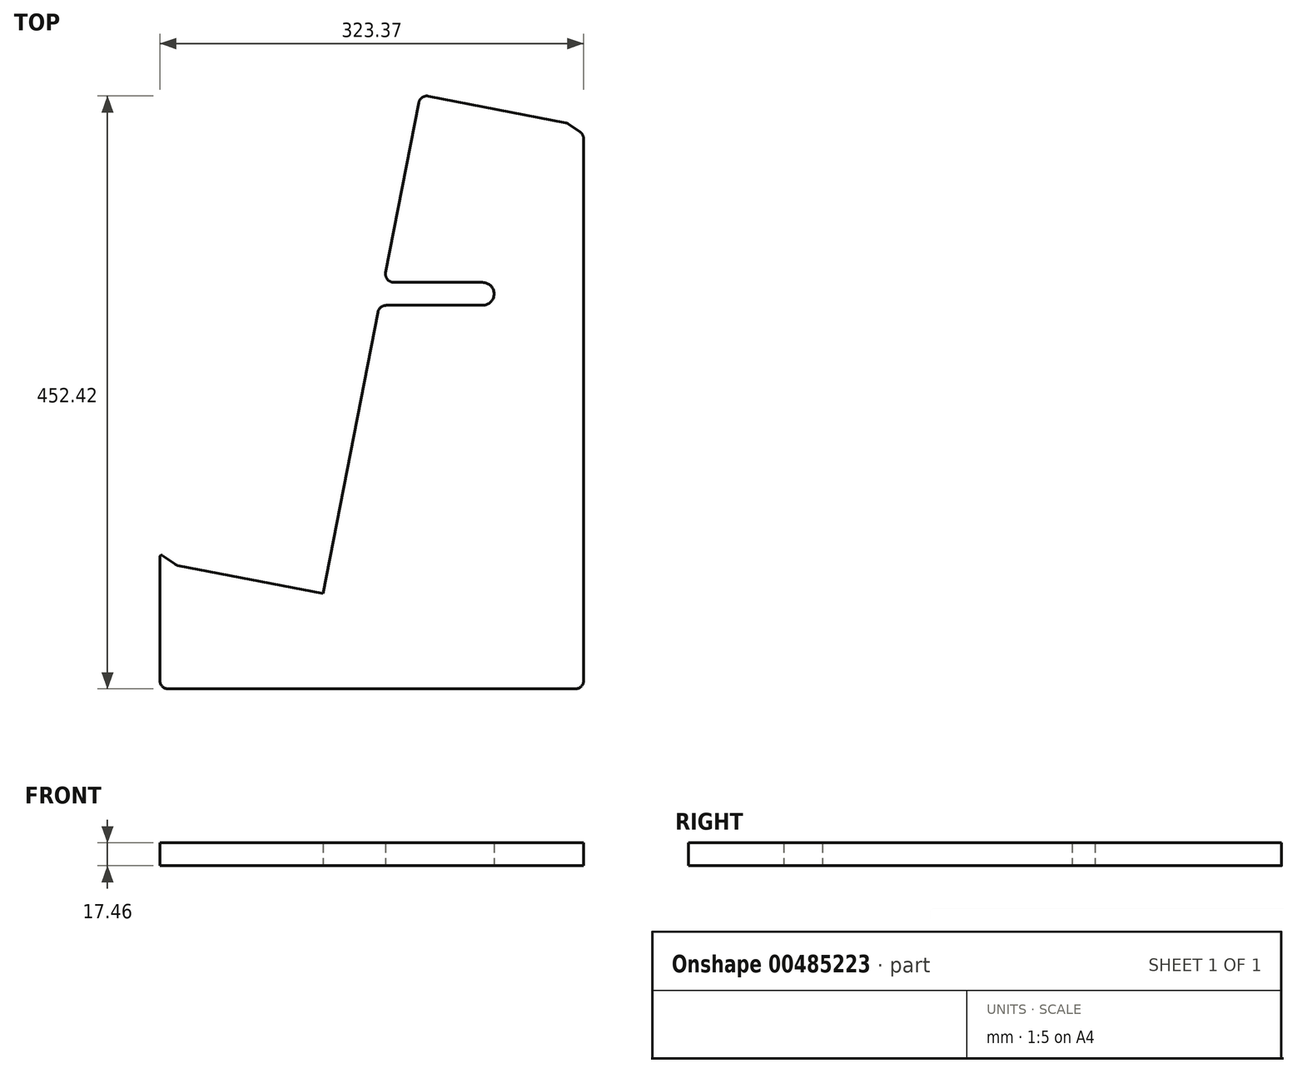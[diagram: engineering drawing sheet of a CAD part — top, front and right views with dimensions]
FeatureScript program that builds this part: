
annotation { "Feature Type Name" : "Feature", "Feature Type Description" : "" }
export const myFeature = defineFeature(function(context is Context, id is Id, definition is map)
    precondition{}
    {
        {
            var Q0;
            Q0=qCreatedBy(makeId("Top.planeOp"),FACE);
            var sketch = newSketch(context, id + "F0", { "sketchPlane" : qUnion([Q0])});
            skLineSegment(sketch, "E0", {"start": v(-95.53, 76.65) * mm, "end": v(-95.53, -96.88) * mm, "construction": true});
            skLineSegment(sketch, "E1", {"start": v(-95.53, -96.88) * mm, "end": v(232.75, -96.88) * mm, "construction": true});
            skLineSegment(sketch, "E2", {"start": v(-95.53, 0) * mm, "end": v(131.9, -44.2) * mm, "construction": true});
            skPoint(sketch, "E3", {"position": v(29.14, -24.23) * mm});
            skLineSegment(sketch, "E4", {"start": v(29.14, -24.23) * mm, "end": v(177.2, 737.5) * mm, "construction": true});
            skPoint(sketch, "E5", {"position": v(-83.06, -2.42) * mm});
            skPoint(sketch, "E6", {"position": v(-95.53, 6.35) * mm});
            skLineSegment(sketch, "E7", {"start": v(50.97, 195.8) * mm, "end": v(227.84, 195.8) * mm, "construction": true});
            skLineSegment(sketch, "E8", {"start": v(55.86, 213.27) * mm, "end": v(227.84, 213.27) * mm, "construction": true});
            skPoint(sketch, "E9", {"position": v(71.91, 195.8) * mm});
            skPoint(sketch, "E10", {"position": v(75.3, 213.27) * mm});
            skPoint(sketch, "E11", {"position": v(103.17, 356.63) * mm});
            skLineSegment(sketch, "E12", {"start": v(103.17, 356.63) * mm, "end": v(227.84, 332.4) * mm, "construction": true});
            skLineSegment(sketch, "E13", {"start": v(227.84, 332.4) * mm, "end": v(227.84, -191.89) * mm, "construction": true});
            skLineSegment(sketch, "E14", {"start": v(241.78, 204.54) * mm, "end": v(61.61, 204.54) * mm, "construction": true});
            skPoint(sketch, "E15", {"position": v(73.6, 204.54) * mm});
            skPoint(sketch, "E16", {"position": v(227.84, 204.54) * mm});
            skPoint(sketch, "E17", {"position": v(150.73, 204.54) * mm});
            skArc(sketch, "E18", {"start": v(150.73, 195.8) * mm, "mid": v(159.46, 204.54) * mm, "end": v(150.73, 213.27) * mm});
            skLineSegment(sketch, "E19", {"start": v(-93.53, 4.94) * mm, "end": v(-84.17, -1.64) * mm});
            skLineSegment(sketch, "E20", {"start": v(-95.53, 3.9) * mm, "end": v(-95.53, -90.53) * mm});
            skLineSegment(sketch, "E21", {"start": v(-81.73, -2.68) * mm, "end": v(29.14, -24.23) * mm});
            skLineSegment(sketch, "E22", {"start": v(70.91, 190.67) * mm, "end": v(29.14, -24.23) * mm});
            skLineSegment(sketch, "E23", {"start": v(77.15, 195.8) * mm, "end": v(150.73, 195.8) * mm});
            skLineSegment(sketch, "E24", {"start": v(150.73, 213.27) * mm, "end": v(83, 213.27) * mm});
            skPoint(sketch, "E25", {"position": v(227.84, 326.05) * mm});
            skPoint(sketch, "E26", {"position": v(215.37, 334.82) * mm});
            skLineSegment(sketch, "E27", {"start": v(225.14, 327.95) * mm, "end": v(216.48, 334.04) * mm});
            skLineSegment(sketch, "E28", {"start": v(214.04, 335.08) * mm, "end": v(109.4, 355.42) * mm});
            skLineSegment(sketch, "E29", {"start": v(101.96, 350.4) * mm, "end": v(76.78, 220.83) * mm});
            skLineSegment(sketch, "E30", {"start": v(227.84, 322.75) * mm, "end": v(227.84, -90.53) * mm});
            skLineSegment(sketch, "E31", {"start": v(-89.18, -96.88) * mm, "end": v(221.49, -96.88) * mm});
            skArc(sketch, "E32.filletArc", {"start": v(77.15, 195.8) * mm, "mid": v(73.1, 194.35) * mm, "end": v(70.91, 190.67) * mm});
            skArc(sketch, "E33.filletArc", {"start": v(76.78, 220.83) * mm, "mid": v(78.1, 215.58) * mm, "end": v(83, 213.27) * mm});
            skArc(sketch, "E34.filletArc", {"start": v(109.4, 355.42) * mm, "mid": v(104.64, 354.45) * mm, "end": v(101.96, 350.4) * mm});
            skArc(sketch, "E35.filletArc", {"start": v(216.48, 334.04) * mm, "mid": v(215.32, 334.7) * mm, "end": v(214.04, 335.08) * mm});
            skArc(sketch, "E36.filletArc", {"start": v(227.84, 322.75) * mm, "mid": v(227.13, 325.68) * mm, "end": v(225.14, 327.95) * mm});
            skPoint(sketch, "E37.visualSharp", {"position": v(227.84, -96.88) * mm});
            skArc(sketch, "E37.filletArc", {"start": v(221.49, -96.88) * mm, "mid": v(225.98, -95.02) * mm, "end": v(227.84, -90.53) * mm});
            skPoint(sketch, "E38.visualSharp", {"position": v(-95.53, -96.88) * mm});
            skArc(sketch, "E38.filletArc", {"start": v(-95.53, -90.53) * mm, "mid": v(-93.67, -95.02) * mm, "end": v(-89.18, -96.88) * mm});
            skArc(sketch, "E39.filletArc", {"start": v(-93.53, 4.94) * mm, "mid": v(-94.84, 5.03) * mm, "end": v(-95.53, 3.9) * mm});
            skArc(sketch, "E40.filletArc", {"start": v(-84.17, -1.64) * mm, "mid": v(-83, -2.3) * mm, "end": v(-81.73, -2.68) * mm});
            skSolve(sketch);
        }
        {
            var Q0;
            Q0 = qSketchRegion(id + "F0", true);
            extrude(context, id + "F1", {"entities" : qUnion([Q0]), "depth" : 17.46 * mm});
        }
        {
            var Q0;
            Q0=makeQuery(id+"F1.opExtrude","SWEPT_BODY",BODY,{"disambiguationData":[OSD([sQuery(id+"F0.wireOp",EDGE,"E18"),sQuery(id+"F0.wireOp",EDGE,"E19"),sQuery(id+"F0.wireOp",EDGE,"E20"),sQuery(id+"F0.wireOp",EDGE,"E21"),sQuery(id+"F0.wireOp",EDGE,"E22"),sQuery(id+"F0.wireOp",EDGE,"E23"),sQuery(id+"F0.wireOp",EDGE,"E24"),sQuery(id+"F0.wireOp",EDGE,"E27"),sQuery(id+"F0.wireOp",EDGE,"E28"),sQuery(id+"F0.wireOp",EDGE,"E29"),sQuery(id+"F0.wireOp",EDGE,"E30"),sQuery(id+"F0.wireOp",EDGE,"E31"),sQuery(id+"F0.wireOp",EDGE,"E32.filletArc"),sQuery(id+"F0.wireOp",EDGE,"E33.filletArc"),sQuery(id+"F0.wireOp",EDGE,"E34.filletArc"),sQuery(id+"F0.wireOp",EDGE,"E35.filletArc"),sQuery(id+"F0.wireOp",EDGE,"E36.filletArc"),sQuery(id+"F0.wireOp",EDGE,"E37.filletArc"),sQuery(id+"F0.wireOp",EDGE,"E38.filletArc"),sQuery(id+"F0.wireOp",EDGE,"E39.filletArc"),sQuery(id+"F0.wireOp",EDGE,"E40.filletArc")])]});
            transform(context, id + "F2", {"entities" : qUnion([Q0]), "transformType" : TransformType.TRANSLATION_3D, "dx" : 0 * mm, "dy" : 0 * mm, "dz" : 0 * mm, "makeCopy" : true});
        }
    });
